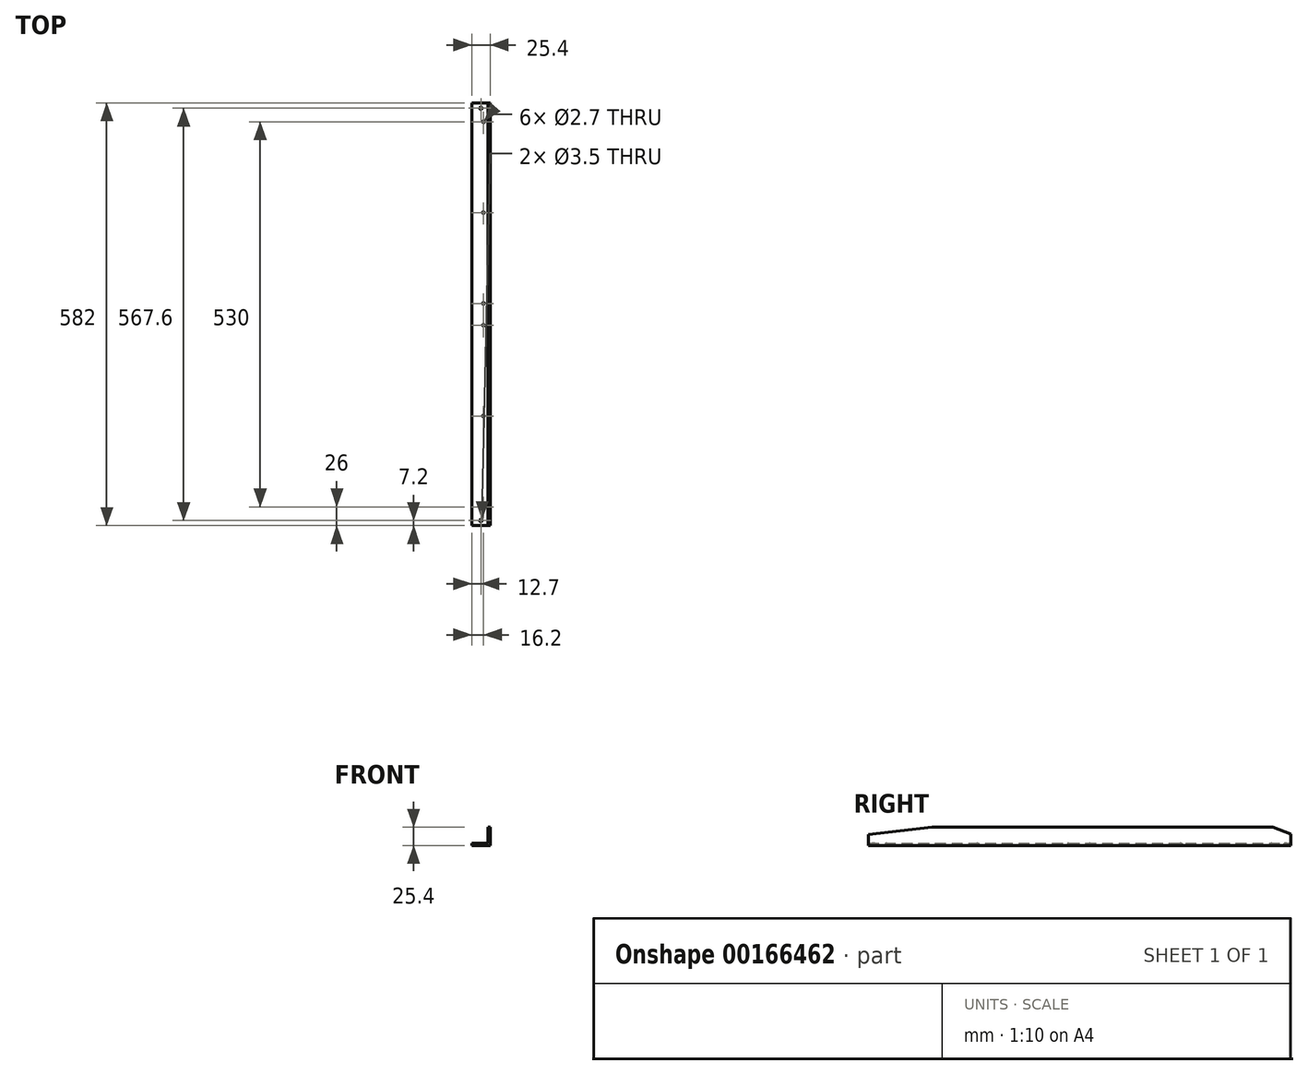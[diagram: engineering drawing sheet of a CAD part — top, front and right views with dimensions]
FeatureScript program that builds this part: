
annotation { "Feature Type Name" : "Feature", "Feature Type Description" : "" }
export const myFeature = defineFeature(function(context is Context, id is Id, definition is map)
    precondition{}
    {
        {
            var Q0;
            Q0=qCreatedBy(makeId("Front.planeOp"),FACE);
            var sketch = newSketch(context, id + "F0", { "sketchPlane" : qUnion([Q0])});
            skLineSegment(sketch, "E0.bottom", {"start": v(22.2, 12.7) * mm, "end": v(25.4, 12.7) * mm});
            skLineSegment(sketch, "E0.top", {"start": v(0, -12.7) * mm, "end": v(25.4, -12.7) * mm});
            skLineSegment(sketch, "E0.right", {"start": v(25.4, 12.7) * mm, "end": v(25.4, -12.7) * mm});
            skPoint(sketch, "E0.middle", {"position": v(0, 0) * mm});
            skLineSegment(sketch, "E1", {"start": v(0, -9.5) * mm, "end": v(0, -12.7) * mm});
            skPoint(sketch, "E1.endSnap0", {"position": v(0, -12.7) * mm});
            skLineSegment(sketch, "E2", {"start": v(0, -9.5) * mm, "end": v(22.2, -9.5) * mm});
            skLineSegment(sketch, "E3", {"start": v(22.2, -9.5) * mm, "end": v(22.2, 12.7) * mm});
            skPoint(sketch, "E0.left.end.orphan", {"position": v(-25.4, -12.7) * mm});
            skPoint(sketch, "E4.orphan", {"position": v(-25.4, 12.7) * mm});
            skSolve(sketch);
        }
        {
            var Q0;
            Q0=qSketchRegion(id+"F0",true);
            extrude(context, id + "F1", {"entities" : qUnion([Q0]), "endBound" : BoundingType.SYMMETRIC, "depth" : 582 * mm});
        }
        {
            var Q0;
            Q0=makeQuery(id+"F1.opExtrude","CAP_FACE",FACE,{"disambiguationData":[OSD([sQuery(id+"F0.wireOp",EDGE,"E0.bottom"),sQuery(id+"F0.wireOp",EDGE,"E0.top"),sQuery(id+"F0.wireOp",EDGE,"E0.right"),sQuery(id+"F0.wireOp",EDGE,"E1"),sQuery(id+"F0.wireOp",EDGE,"E2"),sQuery(id+"F0.wireOp",EDGE,"E3")])],"isStart":false});
            var sketch = newSketch(context, id + "F2", { "sketchPlane" : qUnion([Q0])});
            skLineSegment(sketch, "E5.bottom", {"start": v(22.2, 12.7) * mm, "end": v(25.4, 12.7) * mm});
            skLineSegment(sketch, "E5.top", {"start": v(22.2, 7.7) * mm, "end": v(25.4, 7.7) * mm});
            skLineSegment(sketch, "E5.left", {"start": v(22.2, 12.7) * mm, "end": v(22.2, 7.7) * mm});
            skLineSegment(sketch, "E5.right", {"start": v(25.4, 12.7) * mm, "end": v(25.4, 7.7) * mm});
            skSolve(sketch);
        }
        {
            var Q0;
            Q0=makeQuery(id+"F1.opExtrude","SWEPT_FACE",FACE,{"disambiguationData":[OSD([sQuery(id+"F0.wireOp",EDGE,"E0.top")])]});
            var sketch = newSketch(context, id + "F3", { "sketchPlane" : qUnion([Q0])});
            skLineSegment(sketch, "E6.bottom", {"start": v(25.4, 279.6) * mm, "end": v(16.2, 279.6) * mm, "construction": true});
            skLineSegment(sketch, "E6.top", {"start": v(25.4, -279.6) * mm, "end": v(16.2, -279.6) * mm, "construction": true});
            skLineSegment(sketch, "E6.left", {"start": v(25.4, 279.6) * mm, "end": v(25.4, -279.6) * mm, "construction": true});
            skLineSegment(sketch, "E6.right", {"start": v(16.2, 279.6) * mm, "end": v(16.2, -279.6) * mm, "construction": true});
            skCircle(sketch, "E7", {"center": v(16.2, 15) * mm, "radius": 1.35 * mm});
            skCircle(sketch, "E8", {"center": v(16.2, -15) * mm, "radius": 1.35 * mm});
            skCircle(sketch, "E9", {"center": v(16.2, 140) * mm, "radius": 1.35 * mm});
            skCircle(sketch, "E10", {"center": v(16.2, 265) * mm, "radius": 1.35 * mm});
            skCircle(sketch, "E11", {"center": v(16.2, -140) * mm, "radius": 1.35 * mm});
            skCircle(sketch, "E12", {"center": v(16.2, -265) * mm, "radius": 1.35 * mm});
            skSolve(sketch);
        }
        {
            var Q0;
            Q0=makeQuery(id+"F1.opExtrude","CAP_EDGE",EDGE,{"disambiguationData":[OSD([sQuery(id+"F0.wireOp",EDGE,"E0.bottom")])],"isStart":true});
            chamfer(context, id + "F4", {"entities" : qUnion([Q0]), "chamferType" : ChamferType.TWO_OFFSETS, "width1" : 9.5 * mm, "oppositeDirection" : false, "width2" : 25 * mm, "tangentPropagation" : true});
        }
        {
            var Q0;
            Q0=makeQuery(id+"F1.opExtrude","CAP_EDGE",EDGE,{"disambiguationData":[OSD([sQuery(id+"F0.wireOp",EDGE,"E0.bottom")])],"isStart":false});
            chamfer(context, id + "F5", {"entities" : qUnion([Q0]), "chamferType" : ChamferType.TWO_OFFSETS, "width1" : 88 * mm, "oppositeDirection" : false, "width2" : 10.1 * mm, "tangentPropagation" : true});
        }
        {
            var Q0;
            Q0=makeQuery(id+"F1.opExtrude","SWEPT_FACE",FACE,{"disambiguationData":[OSD([sQuery(id+"F0.wireOp",EDGE,"E2")])]});
            var sketch = newSketch(context, id + "F6", { "sketchPlane" : qUnion([Q0])});
            skSolve(sketch);
        }
        {
            var Q0;
            {var subQ0=sQuery(id+"F0.wireOp",EDGE,"E2");Q0=makeQuery(id+"F6.imprint","IMPRINT",FACE,{"disambiguationData":[TD([[makeQuery(id+"F6.imprint","IMPRINT",EDGE,{"derivedFrom":makeQuery(id+"F1.opExtrude","CAP_EDGE",EDGE,{"disambiguationData":[OSD([subQ0])],"isStart":true})}),-1.0]])]});}
            var sketch = newSketch(context, id + "F7", { "sketchPlane" : qUnion([Q0])});
            skCircle(sketch, "E13", {"center": v(12.7, -283.8) * mm, "radius": 1.75 * mm});
            skCircle(sketch, "E14.MirrorC", {"center": v(12.7, 283.8) * mm, "radius": 1.75 * mm});
            skSolve(sketch);
        }
        {
            var Q0;
            Q0=qSketchRegion(id+"F7",true);
            extrude(context, id + "F8", {"entities" : qUnion([Q0]), "operationType" : NewBodyOperationType.REMOVE, "endBound" : BoundingType.UP_TO_NEXT, "oppositeDirection" : true, "depth" : 25 * mm});
        }
        {
            var Q0;
            Q0 = qSketchRegion(id + "F3", true);
            extrude(context, id + "F9", {"entities" : qUnion([Q0]), "operationType" : NewBodyOperationType.REMOVE, "oppositeDirection" : true, "depth" : 25 * mm});
        }
    });
